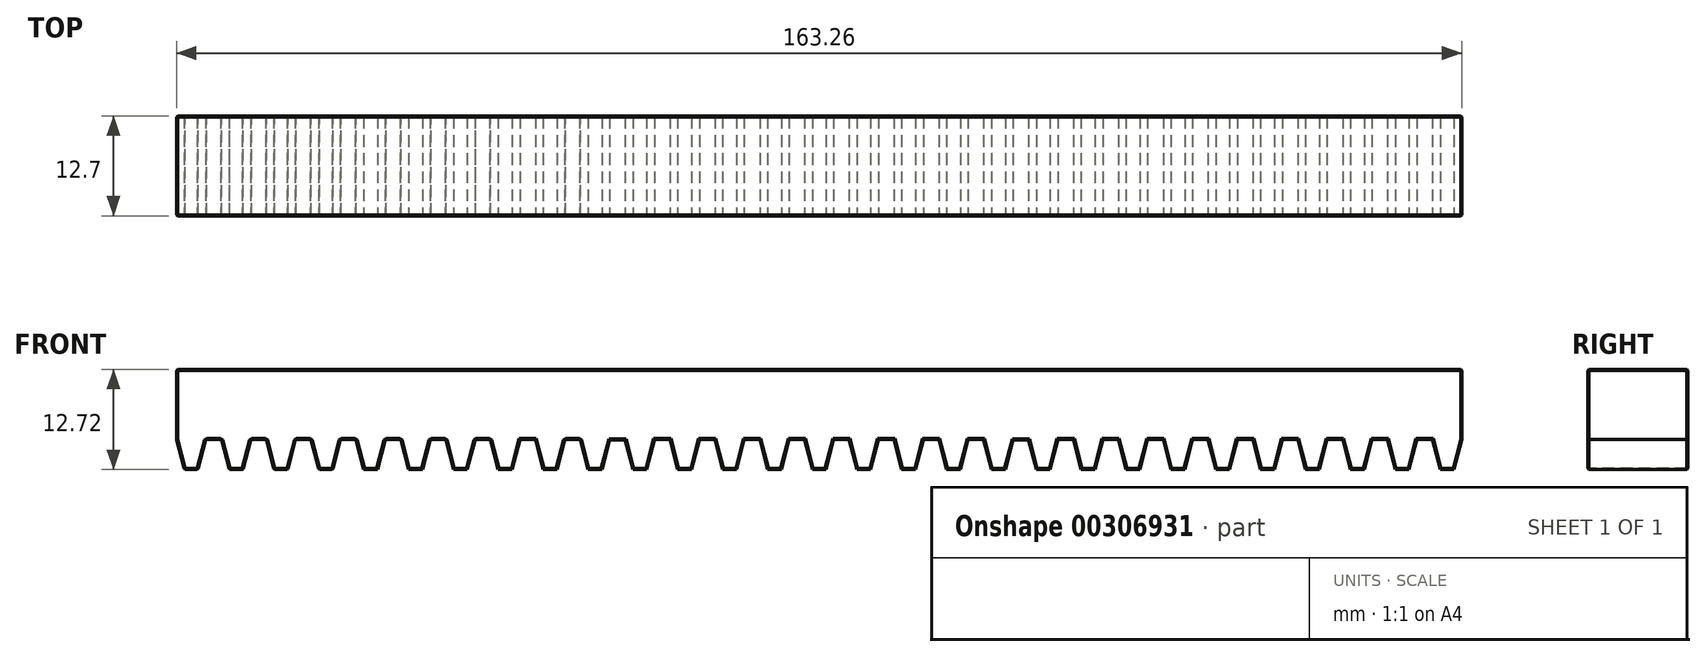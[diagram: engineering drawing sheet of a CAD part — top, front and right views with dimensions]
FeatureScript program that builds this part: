
annotation { "Feature Type Name" : "Feature", "Feature Type Description" : "" }
export const myFeature = defineFeature(function(context is Context, id is Id, definition is map)
    precondition{}
    {
        {
            var Q0;
            Q0=qCreatedBy(makeId("Front.planeOp"),FACE);
            var sketch = newSketch(context, id + "F0", { "sketchPlane" : qUnion([Q0])});
            skLineSegment(sketch, "E0.top", {"start": v(26.49, 6.35) * mm, "end": v(-136.77, 6.35) * mm});
            skLineSegment(sketch, "E0.left", {"start": v(152.4, -6.35) * mm, "end": v(152.4, 6.35) * mm});
            skPoint(sketch, "E0.middle", {"position": v(0, 0) * mm});
            skLineSegment(sketch, "E1", {"start": v(-95.96, -15.55) * mm, "end": v(-95.96, -16.34) * mm});
            skLineSegment(sketch, "E2", {"start": v(-95.96, -16.34) * mm, "end": v(-95.96, -17.1) * mm});
            skLineSegment(sketch, "E3", {"start": v(-95.96, -17.1) * mm, "end": v(-96.35, -18.17) * mm});
            skLineSegment(sketch, "E4", {"start": v(-96.35, -18.17) * mm, "end": v(-96.56, -18.75) * mm});
            skLineSegment(sketch, "E5", {"start": v(-96.56, -18.75) * mm, "end": v(-97.98, -18.75) * mm});
            skLineSegment(sketch, "E6", {"start": v(-97.98, -18.75) * mm, "end": v(-98.54, -17.62) * mm});
            skLineSegment(sketch, "E7", {"start": v(-98.54, -17.62) * mm, "end": v(-98.72, -17.01) * mm});
            skLineSegment(sketch, "E8", {"start": v(-98.72, -17.01) * mm, "end": v(-98.73, -16.25) * mm});
            skLineSegment(sketch, "E9", {"start": v(-98.73, -16.25) * mm, "end": v(-98.73, -15.44) * mm});
            skLineSegment(sketch, "E10", {"start": v(-134.03, -6.35) * mm, "end": v(-133.05, -2.54) * mm});
            skLineSegment(sketch, "E11", {"start": v(-133.05, -2.54) * mm, "end": v(-131.07, -2.54) * mm});
            skLineSegment(sketch, "E12", {"start": v(-131.07, -2.54) * mm, "end": v(-130.09, -6.35) * mm});
            skLineSegment(sketch, "E13", {"start": v(-127.35, -2.54) * mm, "end": v(-126.2, -2.54) * mm});
            skLineSegment(sketch, "E14", {"start": v(-127.35, -2.54) * mm, "end": v(-125.37, -2.54) * mm});
            skLineSegment(sketch, "E15.1.0.0", {"start": v(-124.39, -6.37) * mm, "end": v(-123.54, -6.37) * mm});
            skLineSegment(sketch, "E16", {"start": v(-128.33, -6.37) * mm, "end": v(-127.35, -2.56) * mm});
            skLineSegment(sketch, "E17", {"start": v(-127.35, -2.56) * mm, "end": v(-125.37, -2.56) * mm});
            skLineSegment(sketch, "E18", {"start": v(-125.37, -2.56) * mm, "end": v(-124.39, -6.37) * mm});
            skLineSegment(sketch, "E19", {"start": v(-123.54, -6.37) * mm, "end": v(-122.63, -6.37) * mm});
            skLineSegment(sketch, "E20.1.0.0", {"start": v(-118.69, -6.37) * mm, "end": v(-117.84, -6.37) * mm});
            skLineSegment(sketch, "E21", {"start": v(-122.63, -6.37) * mm, "end": v(-121.65, -2.56) * mm});
            skLineSegment(sketch, "E22", {"start": v(-121.65, -2.56) * mm, "end": v(-119.67, -2.56) * mm});
            skLineSegment(sketch, "E23", {"start": v(-119.67, -2.56) * mm, "end": v(-118.69, -6.37) * mm});
            skLineSegment(sketch, "E24", {"start": v(-117.84, -6.35) * mm, "end": v(-116.93, -6.37) * mm});
            skLineSegment(sketch, "E25.1.0.0", {"start": v(-112.99, -6.37) * mm, "end": v(-112.14, -6.37) * mm});
            skLineSegment(sketch, "E26", {"start": v(-116.93, -6.37) * mm, "end": v(-115.95, -2.56) * mm});
            skLineSegment(sketch, "E27", {"start": v(-115.95, -2.56) * mm, "end": v(-113.97, -2.56) * mm});
            skLineSegment(sketch, "E28", {"start": v(-113.97, -2.56) * mm, "end": v(-112.99, -6.37) * mm});
            skLineSegment(sketch, "E29", {"start": v(-136.77, -2.56) * mm, "end": v(-135.8, -6.33) * mm});
            skLineSegment(sketch, "E30", {"start": v(-112.14, -6.35) * mm, "end": v(-111.23, -6.37) * mm});
            skLineSegment(sketch, "E31.1.0.0", {"start": v(-107.3, -6.37) * mm, "end": v(-106.44, -6.37) * mm});
            skLineSegment(sketch, "E32", {"start": v(-111.23, -6.37) * mm, "end": v(-110.25, -2.56) * mm});
            skLineSegment(sketch, "E33", {"start": v(-110.25, -2.56) * mm, "end": v(-108.28, -2.56) * mm});
            skLineSegment(sketch, "E34", {"start": v(-108.28, -2.56) * mm, "end": v(-107.3, -6.37) * mm});
            skPoint(sketch, "E35.startSnap0", {"position": v(-109.26, -2.56) * mm});
            skLineSegment(sketch, "E36", {"start": v(-106.44, -6.35) * mm, "end": v(-105.53, -6.37) * mm});
            skLineSegment(sketch, "E37.1.0.0", {"start": v(-101.6, -6.37) * mm, "end": v(-100.74, -6.37) * mm});
            skLineSegment(sketch, "E38", {"start": v(-105.53, -6.37) * mm, "end": v(-104.55, -2.56) * mm});
            skLineSegment(sketch, "E39", {"start": v(-104.55, -2.56) * mm, "end": v(-102.58, -2.56) * mm});
            skLineSegment(sketch, "E40", {"start": v(-102.58, -2.56) * mm, "end": v(-101.6, -6.37) * mm});
            skPoint(sketch, "E41.startSnap0", {"position": v(-103.56, -2.56) * mm});
            skLineSegment(sketch, "E42", {"start": v(-100.74, -6.35) * mm, "end": v(-99.83, -6.37) * mm});
            skLineSegment(sketch, "E43.1.0.0", {"start": v(-95.9, -6.37) * mm, "end": v(-95.04, -6.37) * mm});
            skLineSegment(sketch, "E44", {"start": v(-99.83, -6.37) * mm, "end": v(-98.85, -2.56) * mm});
            skLineSegment(sketch, "E45", {"start": v(-98.85, -2.56) * mm, "end": v(-96.88, -2.56) * mm});
            skLineSegment(sketch, "E46", {"start": v(-96.88, -2.56) * mm, "end": v(-95.9, -6.37) * mm});
            skPoint(sketch, "E47.startSnap0", {"position": v(-97.86, -2.56) * mm});
            skLineSegment(sketch, "E48", {"start": v(-95.04, -6.35) * mm, "end": v(-94.13, -6.37) * mm});
            skLineSegment(sketch, "E49.1.0.0", {"start": v(-90.2, -6.37) * mm, "end": v(-89.34, -6.37) * mm});
            skLineSegment(sketch, "E50", {"start": v(-94.13, -6.37) * mm, "end": v(-93.15, -2.56) * mm});
            skLineSegment(sketch, "E51", {"start": v(-93.15, -2.56) * mm, "end": v(-91.18, -2.56) * mm});
            skLineSegment(sketch, "E52", {"start": v(-91.18, -2.56) * mm, "end": v(-90.2, -6.37) * mm});
            skPoint(sketch, "E53.startSnap0", {"position": v(-92.16, -2.56) * mm});
            skLineSegment(sketch, "E54", {"start": v(-89.34, -6.35) * mm, "end": v(-88.43, -6.37) * mm});
            skLineSegment(sketch, "E55.1.0.0", {"start": v(-84.5, -6.37) * mm, "end": v(-83.64, -6.37) * mm});
            skLineSegment(sketch, "E56", {"start": v(-88.43, -6.37) * mm, "end": v(-87.45, -2.56) * mm});
            skLineSegment(sketch, "E57", {"start": v(-87.45, -2.56) * mm, "end": v(-85.48, -2.56) * mm});
            skLineSegment(sketch, "E58", {"start": v(-85.48, -2.56) * mm, "end": v(-84.5, -6.37) * mm});
            skPoint(sketch, "E59.startSnap0", {"position": v(-86.46, -2.56) * mm});
            skLineSegment(sketch, "E60", {"start": v(-83.64, -6.37) * mm, "end": v(-82.73, -6.39) * mm});
            skLineSegment(sketch, "E61.1.0.0", {"start": v(-78.8, -6.39) * mm, "end": v(-77.94, -6.39) * mm});
            skLineSegment(sketch, "E62", {"start": v(-82.73, -6.39) * mm, "end": v(-81.75, -2.58) * mm});
            skLineSegment(sketch, "E63", {"start": v(-81.75, -2.58) * mm, "end": v(-79.78, -2.58) * mm});
            skLineSegment(sketch, "E64", {"start": v(-79.78, -2.58) * mm, "end": v(-78.8, -6.39) * mm});
            skPoint(sketch, "E65.startSnap0", {"position": v(-80.76, -2.58) * mm});
            skLineSegment(sketch, "E66", {"start": v(-77.94, -6.35) * mm, "end": v(-77.04, -6.37) * mm});
            skLineSegment(sketch, "E67.1.0.0", {"start": v(-73.1, -6.37) * mm, "end": v(-72.24, -6.37) * mm});
            skLineSegment(sketch, "E68", {"start": v(-77.04, -6.37) * mm, "end": v(-76.05, -2.56) * mm});
            skLineSegment(sketch, "E69", {"start": v(-76.05, -2.56) * mm, "end": v(-74.08, -2.56) * mm});
            skLineSegment(sketch, "E70", {"start": v(-74.08, -2.56) * mm, "end": v(-73.1, -6.37) * mm});
            skPoint(sketch, "E71.startSnap0", {"position": v(-75.06, -2.56) * mm});
            skLineSegment(sketch, "E72", {"start": v(-72.24, -6.35) * mm, "end": v(-71.34, -6.37) * mm});
            skLineSegment(sketch, "E73.1.0.0", {"start": v(-67.4, -6.37) * mm, "end": v(-66.54, -6.37) * mm});
            skLineSegment(sketch, "E74", {"start": v(-71.34, -6.37) * mm, "end": v(-70.35, -2.56) * mm});
            skLineSegment(sketch, "E75", {"start": v(-70.35, -2.56) * mm, "end": v(-68.38, -2.56) * mm});
            skLineSegment(sketch, "E76", {"start": v(-68.38, -2.56) * mm, "end": v(-67.4, -6.37) * mm});
            skPoint(sketch, "E77.startSnap0", {"position": v(-69.36, -2.56) * mm});
            skLineSegment(sketch, "E78", {"start": v(-66.54, -6.35) * mm, "end": v(-65.64, -6.37) * mm});
            skLineSegment(sketch, "E79.1.0.0", {"start": v(-61.7, -6.37) * mm, "end": v(-60.84, -6.37) * mm});
            skLineSegment(sketch, "E80", {"start": v(-65.64, -6.37) * mm, "end": v(-64.65, -2.56) * mm});
            skLineSegment(sketch, "E81", {"start": v(-64.65, -2.56) * mm, "end": v(-62.68, -2.56) * mm});
            skLineSegment(sketch, "E82", {"start": v(-62.68, -2.56) * mm, "end": v(-61.7, -6.37) * mm});
            skPoint(sketch, "E83.startSnap0", {"position": v(-63.66, -2.56) * mm});
            skLineSegment(sketch, "E84", {"start": v(-60.84, -6.35) * mm, "end": v(-59.94, -6.37) * mm});
            skLineSegment(sketch, "E85.1.0.0", {"start": v(-56, -6.37) * mm, "end": v(-55.14, -6.37) * mm});
            skLineSegment(sketch, "E86", {"start": v(-59.94, -6.37) * mm, "end": v(-58.95, -2.56) * mm});
            skLineSegment(sketch, "E87", {"start": v(-58.95, -2.56) * mm, "end": v(-56.98, -2.56) * mm});
            skLineSegment(sketch, "E88", {"start": v(-56.98, -2.56) * mm, "end": v(-56, -6.37) * mm});
            skPoint(sketch, "E89.startSnap0", {"position": v(-57.96, -2.56) * mm});
            skLineSegment(sketch, "E90", {"start": v(-55.14, -6.37) * mm, "end": v(-54.24, -6.39) * mm});
            skLineSegment(sketch, "E91", {"start": v(-54.24, -6.39) * mm, "end": v(-53.25, -2.58) * mm});
            skLineSegment(sketch, "E92.trimOffspring", {"start": v(-116.93, -6.35) * mm, "end": v(-117.84, -6.35) * mm});
            skLineSegment(sketch, "E93.trimOffspring", {"start": v(-111.23, -6.35) * mm, "end": v(-113, -6.35) * mm});
            skLineSegment(sketch, "E94.trimOffspring", {"start": v(-105.53, -6.35) * mm, "end": v(-107.3, -6.35) * mm});
            skLineSegment(sketch, "E95.trimOffspring", {"start": v(-99.83, -6.35) * mm, "end": v(-101.6, -6.35) * mm});
            skLineSegment(sketch, "E96.trimOffspring", {"start": v(-94.13, -6.35) * mm, "end": v(-95.9, -6.35) * mm});
            skLineSegment(sketch, "E97.trimOffspring", {"start": v(-88.43, -6.35) * mm, "end": v(-90.2, -6.35) * mm});
            skLineSegment(sketch, "E98.trimOffspring", {"start": v(-82.73, -6.35) * mm, "end": v(-84.5, -6.35) * mm});
            skLineSegment(sketch, "E99.trimOffspring", {"start": v(-77.03, -6.35) * mm, "end": v(-78.8, -6.35) * mm});
            skLineSegment(sketch, "E100.trimOffspring", {"start": v(-71.33, -6.35) * mm, "end": v(-73.1, -6.35) * mm});
            skLineSegment(sketch, "E101.trimOffspring", {"start": v(-65.63, -6.35) * mm, "end": v(-67.4, -6.35) * mm});
            skLineSegment(sketch, "E102.trimOffspring", {"start": v(-59.93, -6.35) * mm, "end": v(-61.7, -6.35) * mm});
            skLineSegment(sketch, "E103.trimOffspring", {"start": v(-54.23, -6.35) * mm, "end": v(-56, -6.35) * mm});
            skLineSegment(sketch, "E104.trimOffspring", {"start": v(-124.4, -6.35) * mm, "end": v(-122.63, -6.35) * mm});
            skLineSegment(sketch, "E105.trimOffspring", {"start": v(-118.7, -6.35) * mm, "end": v(-116.93, -6.35) * mm});
            skLineSegment(sketch, "E106.trimOffspring", {"start": v(-113, -6.35) * mm, "end": v(-111.23, -6.35) * mm});
            skLineSegment(sketch, "E107.trimOffspring", {"start": v(-107.3, -6.35) * mm, "end": v(-105.53, -6.35) * mm});
            skLineSegment(sketch, "E108.trimOffspring", {"start": v(-101.6, -6.35) * mm, "end": v(-99.83, -6.35) * mm});
            skLineSegment(sketch, "E109.trimOffspring", {"start": v(-95.9, -6.35) * mm, "end": v(-94.13, -6.35) * mm});
            skLineSegment(sketch, "E110.trimOffspring", {"start": v(-90.2, -6.35) * mm, "end": v(-88.43, -6.35) * mm});
            skLineSegment(sketch, "E111.trimOffspring", {"start": v(-84.5, -6.35) * mm, "end": v(-82.73, -6.35) * mm});
            skLineSegment(sketch, "E112.trimOffspring", {"start": v(-78.8, -6.35) * mm, "end": v(-77.03, -6.35) * mm});
            skLineSegment(sketch, "E113.trimOffspring", {"start": v(-73.1, -6.35) * mm, "end": v(-71.33, -6.35) * mm});
            skLineSegment(sketch, "E114.trimOffspring", {"start": v(-67.4, -6.35) * mm, "end": v(-65.63, -6.35) * mm});
            skLineSegment(sketch, "E115.trimOffspring", {"start": v(-61.7, -6.35) * mm, "end": v(-59.93, -6.35) * mm});
            skLineSegment(sketch, "E116.trimOffspring", {"start": v(-56, -6.35) * mm, "end": v(-54.23, -6.35) * mm});
            skLineSegment(sketch, "E117", {"start": v(-136.77, -2.56) * mm, "end": v(-136.77, 6.35) * mm});
            skLineSegment(sketch, "E118", {"start": v(-53.25, -2.58) * mm, "end": v(-53.25, -2.56) * mm});
            skLineSegment(sketch, "E119", {"start": v(-135.8, -6.33) * mm, "end": v(-134.03, -6.35) * mm});
            skLineSegment(sketch, "E120", {"start": v(-130.09, -6.35) * mm, "end": v(-128.33, -6.37) * mm});
            skLineSegment(sketch, "E121", {"start": v(-133.78, -3.12) * mm, "end": v(-133.78, -3.91) * mm});
            skLineSegment(sketch, "E122", {"start": v(-133.78, -3.91) * mm, "end": v(-133.78, -4.68) * mm});
            skLineSegment(sketch, "E123", {"start": v(-133.78, -4.68) * mm, "end": v(-134.17, -5.75) * mm});
            skLineSegment(sketch, "E124", {"start": v(-134.17, -5.75) * mm, "end": v(-134.38, -6.33) * mm});
            skLineSegment(sketch, "E125", {"start": v(-134.38, -6.33) * mm, "end": v(-135.8, -6.33) * mm});
            skLineSegment(sketch, "E126", {"start": v(-135.8, -6.33) * mm, "end": v(-136.36, -5.2) * mm});
            skLineSegment(sketch, "E127", {"start": v(-136.36, -5.2) * mm, "end": v(-136.54, -4.6) * mm});
            skLineSegment(sketch, "E128", {"start": v(-136.54, -4.6) * mm, "end": v(-136.55, -3.83) * mm});
            skLineSegment(sketch, "E129", {"start": v(-136.55, -3.83) * mm, "end": v(-136.55, -3.01) * mm});
            skLineSegment(sketch, "E130", {"start": v(-128.08, -3.14) * mm, "end": v(-128.07, -3.93) * mm});
            skLineSegment(sketch, "E131", {"start": v(-128.07, -3.93) * mm, "end": v(-128.07, -4.7) * mm});
            skLineSegment(sketch, "E132", {"start": v(-128.07, -4.7) * mm, "end": v(-128.47, -5.76) * mm});
            skLineSegment(sketch, "E133", {"start": v(-128.47, -5.76) * mm, "end": v(-128.67, -6.35) * mm});
            skLineSegment(sketch, "E134", {"start": v(-128.67, -6.35) * mm, "end": v(-130.09, -6.35) * mm});
            skLineSegment(sketch, "E135", {"start": v(-130.09, -6.35) * mm, "end": v(-130.65, -5.21) * mm});
            skLineSegment(sketch, "E136", {"start": v(-130.65, -5.21) * mm, "end": v(-130.84, -4.6) * mm});
            skLineSegment(sketch, "E137", {"start": v(-130.84, -4.6) * mm, "end": v(-130.84, -3.84) * mm});
            skLineSegment(sketch, "E138", {"start": v(-130.84, -3.84) * mm, "end": v(-130.84, -3.03) * mm});
            skLineSegment(sketch, "E139", {"start": v(-122.38, -3.16) * mm, "end": v(-122.37, -3.95) * mm});
            skLineSegment(sketch, "E140", {"start": v(-122.37, -3.95) * mm, "end": v(-122.37, -4.71) * mm});
            skLineSegment(sketch, "E141", {"start": v(-122.37, -4.71) * mm, "end": v(-122.77, -5.78) * mm});
            skLineSegment(sketch, "E142", {"start": v(-122.77, -5.78) * mm, "end": v(-122.97, -6.36) * mm});
            skLineSegment(sketch, "E143", {"start": v(-122.97, -6.36) * mm, "end": v(-124.39, -6.37) * mm});
            skLineSegment(sketch, "E144", {"start": v(-124.39, -6.37) * mm, "end": v(-124.95, -5.23) * mm});
            skLineSegment(sketch, "E145", {"start": v(-124.95, -5.23) * mm, "end": v(-125.14, -4.63) * mm});
            skLineSegment(sketch, "E146", {"start": v(-125.14, -4.63) * mm, "end": v(-125.14, -3.86) * mm});
            skLineSegment(sketch, "E147", {"start": v(-125.14, -3.86) * mm, "end": v(-125.14, -3.05) * mm});
            skLineSegment(sketch, "E148", {"start": v(-116.68, -3.16) * mm, "end": v(-116.67, -3.95) * mm});
            skLineSegment(sketch, "E149", {"start": v(-116.67, -3.95) * mm, "end": v(-116.67, -4.72) * mm});
            skLineSegment(sketch, "E150", {"start": v(-116.67, -4.72) * mm, "end": v(-117.07, -5.79) * mm});
            skLineSegment(sketch, "E151", {"start": v(-117.07, -5.79) * mm, "end": v(-117.27, -6.37) * mm});
            skLineSegment(sketch, "E152", {"start": v(-117.27, -6.37) * mm, "end": v(-118.69, -6.37) * mm});
            skLineSegment(sketch, "E153", {"start": v(-118.69, -6.37) * mm, "end": v(-119.25, -5.23) * mm});
            skLineSegment(sketch, "E154", {"start": v(-119.25, -5.23) * mm, "end": v(-119.44, -4.63) * mm});
            skLineSegment(sketch, "E155", {"start": v(-119.44, -4.63) * mm, "end": v(-119.44, -3.86) * mm});
            skLineSegment(sketch, "E156", {"start": v(-119.44, -3.86) * mm, "end": v(-119.44, -3.05) * mm});
            skLineSegment(sketch, "E157.MirrorCS", {"start": v(-31.48, -6.35) * mm, "end": v(-33.26, -6.35) * mm});
            skLineSegment(sketch, "E158.MirrorCS", {"start": v(-31.5, -6.39) * mm, "end": v(-32.34, -6.39) * mm});
            skLineSegment(sketch, "E159.MirrorCS", {"start": v(-14.4, -6.35) * mm, "end": v(-16.16, -6.35) * mm});
            skLineSegment(sketch, "E160.MirrorCS", {"start": v(-37.19, -6.35) * mm, "end": v(-38.96, -6.35) * mm});
            skLineSegment(sketch, "E161.MirrorCS", {"start": v(-4.76, -6.35) * mm, "end": v(-3, -6.35) * mm});
            skLineSegment(sketch, "E162.MirrorCS", {"start": v(-8.7, -6.37) * mm, "end": v(-9.54, -6.37) * mm});
            skLineSegment(sketch, "E163.MirrorCS", {"start": v(-20.09, -6.35) * mm, "end": v(-21.86, -6.35) * mm});
            skLineSegment(sketch, "E164.MirrorCS", {"start": v(-16.16, -6.35) * mm, "end": v(-14.4, -6.35) * mm});
            skLineSegment(sketch, "E165.MirrorCS", {"start": v(-42.89, -6.35) * mm, "end": v(-44.65, -6.35) * mm});
            skLineSegment(sketch, "E166.MirrorCS", {"start": v(-38.96, -6.35) * mm, "end": v(-37.19, -6.35) * mm});
            skLineSegment(sketch, "E167.MirrorCS", {"start": v(8.4, -6.35) * mm, "end": v(6.64, -6.35) * mm});
            skLineSegment(sketch, "E168.MirrorCS", {"start": v(-42.9, -6.37) * mm, "end": v(-43.74, -6.37) * mm});
            skLineSegment(sketch, "E169.MirrorCS", {"start": v(-20.94, -6.35) * mm, "end": v(-21.85, -6.37) * mm});
            skLineSegment(sketch, "E170.MirrorCS", {"start": v(-8.7, -6.35) * mm, "end": v(-10.46, -6.35) * mm});
            skLineSegment(sketch, "E171.MirrorCS", {"start": v(0.94, -6.35) * mm, "end": v(2.7, -6.35) * mm});
            skLineSegment(sketch, "E172.MirrorCS", {"start": v(-25.8, -6.37) * mm, "end": v(-26.64, -6.37) * mm});
            skLineSegment(sketch, "E173.MirrorCS", {"start": v(-3.85, -6.35) * mm, "end": v(-4.75, -6.37) * mm});
            skLineSegment(sketch, "E174.MirrorCS", {"start": v(-25.79, -6.35) * mm, "end": v(-27.56, -6.35) * mm});
            skLineSegment(sketch, "E175.MirrorCS", {"start": v(-48.6, -6.37) * mm, "end": v(-49.44, -6.37) * mm});
            skLineSegment(sketch, "E176.MirrorCS", {"start": v(2.7, -6.37) * mm, "end": v(1.85, -6.37) * mm});
            skLineSegment(sketch, "E177.MirrorCS", {"start": v(-48.59, -6.35) * mm, "end": v(-50.35, -6.35) * mm});
            skLineSegment(sketch, "E178.MirrorCS", {"start": v(-33.26, -6.35) * mm, "end": v(-31.48, -6.35) * mm});
            skLineSegment(sketch, "E179.MirrorCS", {"start": v(-32.34, -6.35) * mm, "end": v(-33.25, -6.37) * mm});
            skLineSegment(sketch, "E180.MirrorCS", {"start": v(-10.46, -6.35) * mm, "end": v(-8.7, -6.35) * mm});
            skLineSegment(sketch, "E181.MirrorCS", {"start": v(-43.74, -6.35) * mm, "end": v(-44.65, -6.37) * mm});
            skLineSegment(sketch, "E182.MirrorCS", {"start": v(-27.56, -6.35) * mm, "end": v(-25.79, -6.35) * mm});
            skLineSegment(sketch, "E183.MirrorCS", {"start": v(-50.35, -6.35) * mm, "end": v(-48.59, -6.35) * mm});
            skLineSegment(sketch, "E184.MirrorCS", {"start": v(-44.65, -6.35) * mm, "end": v(-42.89, -6.35) * mm});
            skLineSegment(sketch, "E185.MirrorCS", {"start": v(-49.44, -6.35) * mm, "end": v(-50.35, -6.37) * mm});
            skLineSegment(sketch, "E186.MirrorCS", {"start": v(-37.2, -6.37) * mm, "end": v(-38.04, -6.37) * mm});
            skLineSegment(sketch, "E187.MirrorCS", {"start": v(-15.24, -6.35) * mm, "end": v(-16.15, -6.37) * mm});
            skLineSegment(sketch, "E188.MirrorCS", {"start": v(25.51, -6.33) * mm, "end": v(23.75, -6.35) * mm});
            skLineSegment(sketch, "E189.MirrorCS", {"start": v(-20.1, -6.37) * mm, "end": v(-20.94, -6.37) * mm});
            skLineSegment(sketch, "E190.MirrorCS", {"start": v(1.85, -6.35) * mm, "end": v(0.95, -6.37) * mm});
            skLineSegment(sketch, "E191.MirrorCS", {"start": v(19.8, -6.35) * mm, "end": v(18.05, -6.37) * mm});
            skLineSegment(sketch, "E192.MirrorCS", {"start": v(14.1, -6.35) * mm, "end": v(12.34, -6.35) * mm});
            skLineSegment(sketch, "E193.MirrorCS", {"start": v(-3, -6.37) * mm, "end": v(-3.85, -6.37) * mm});
            skLineSegment(sketch, "E194.MirrorCS", {"start": v(2.7, -6.35) * mm, "end": v(0.94, -6.35) * mm});
            skLineSegment(sketch, "E195.MirrorCS", {"start": v(-38.04, -6.35) * mm, "end": v(-38.95, -6.37) * mm});
            skLineSegment(sketch, "E196.MirrorCS", {"start": v(-26.64, -6.37) * mm, "end": v(-27.55, -6.39) * mm});
            skLineSegment(sketch, "E197.MirrorCS", {"start": v(-21.86, -6.35) * mm, "end": v(-20.09, -6.35) * mm});
            skLineSegment(sketch, "E198.MirrorCS", {"start": v(-9.54, -6.35) * mm, "end": v(-10.45, -6.37) * mm});
            skLineSegment(sketch, "E199.MirrorCS", {"start": v(-14.4, -6.37) * mm, "end": v(-15.24, -6.37) * mm});
            skLineSegment(sketch, "E200.MirrorCS", {"start": v(-54.3, -6.37) * mm, "end": v(-55.14, -6.37) * mm});
            skLineSegment(sketch, "E201.MirrorCS", {"start": v(-3, -6.35) * mm, "end": v(-4.76, -6.35) * mm});
            skLineSegment(sketch, "E202.MirrorCS", {"start": v(17.06, -2.54) * mm, "end": v(15.9, -2.54) * mm});
            skLineSegment(sketch, "E203.MirrorCS", {"start": v(15.09, -2.56) * mm, "end": v(14.1, -6.37) * mm});
            skLineSegment(sketch, "E204.MirrorCS", {"start": v(-39.93, -2.56) * mm, "end": v(-41.9, -2.56) * mm});
            skLineSegment(sketch, "E205.MirrorCS", {"start": v(12.35, -6.37) * mm, "end": v(11.36, -2.56) * mm});
            skLineSegment(sketch, "E206.MirrorCS", {"start": v(-22.84, -2.56) * mm, "end": v(-24.8, -2.56) * mm});
            skLineSegment(sketch, "E207.MirrorCS", {"start": v(-5.74, -2.56) * mm, "end": v(-7.71, -2.56) * mm});
            skLineSegment(sketch, "E208.MirrorCS", {"start": v(11.36, -2.56) * mm, "end": v(9.39, -2.56) * mm});
            skLineSegment(sketch, "E209.MirrorCS", {"start": v(-28.54, -2.58) * mm, "end": v(-30.5, -2.58) * mm});
            skLineSegment(sketch, "E210.MirrorCS", {"start": v(6.65, -6.37) * mm, "end": v(5.66, -2.56) * mm});
            skLineSegment(sketch, "E211.MirrorCS", {"start": v(-11.44, -2.56) * mm, "end": v(-13.41, -2.56) * mm});
            skLineSegment(sketch, "E212.MirrorCS", {"start": v(5.66, -2.56) * mm, "end": v(3.69, -2.56) * mm});
            skLineSegment(sketch, "E213.MirrorCS", {"start": v(26.49, -2.56) * mm, "end": v(25.51, -6.33) * mm});
            skLineSegment(sketch, "E214.MirrorCS", {"start": v(-51.33, -2.56) * mm, "end": v(-53.3, -2.56) * mm});
            skLineSegment(sketch, "E215.MirrorCS", {"start": v(20.79, -2.54) * mm, "end": v(19.8, -6.35) * mm});
            skLineSegment(sketch, "E216.MirrorCS", {"start": v(17.06, -2.54) * mm, "end": v(15.09, -2.54) * mm});
            skLineSegment(sketch, "E217.MirrorCS", {"start": v(23.75, -6.35) * mm, "end": v(22.76, -2.54) * mm});
            skLineSegment(sketch, "E218.MirrorCS", {"start": v(22.76, -2.54) * mm, "end": v(20.79, -2.54) * mm});
            skLineSegment(sketch, "E219.MirrorCS", {"start": v(-34.24, -2.56) * mm, "end": v(-36.2, -2.56) * mm});
            skLineSegment(sketch, "E220.MirrorCS", {"start": v(18.05, -6.37) * mm, "end": v(17.06, -2.56) * mm});
            skLineSegment(sketch, "E221.MirrorCS", {"start": v(-17.14, -2.56) * mm, "end": v(-19.11, -2.56) * mm});
            skLineSegment(sketch, "E222.MirrorCS", {"start": v(17.06, -2.56) * mm, "end": v(15.09, -2.56) * mm});
            skLineSegment(sketch, "E223.MirrorCS", {"start": v(-0.04, -2.56) * mm, "end": v(-2.01, -2.56) * mm});
            skLineSegment(sketch, "E224.MirrorCS", {"start": v(9.39, -2.56) * mm, "end": v(8.4, -6.37) * mm});
            skLineSegment(sketch, "E225.MirrorCS", {"start": v(-45.63, -2.56) * mm, "end": v(-47.6, -2.56) * mm});
            skLineSegment(sketch, "E226.MirrorCS", {"start": v(-21.85, -6.37) * mm, "end": v(-22.84, -2.56) * mm});
            skLineSegment(sketch, "E227.MirrorCS", {"start": v(-41.9, -2.56) * mm, "end": v(-42.9, -6.37) * mm});
            skLineSegment(sketch, "E228.MirrorCS", {"start": v(-4.75, -6.37) * mm, "end": v(-5.74, -2.56) * mm});
            skLineSegment(sketch, "E229.MirrorCS", {"start": v(-24.8, -2.56) * mm, "end": v(-25.8, -6.37) * mm});
            skPoint(sketch, "E230.MirrorP", {"position": v(-12.42, -2.56) * mm});
            skLineSegment(sketch, "E231.MirrorCS", {"start": v(-10.45, -6.37) * mm, "end": v(-11.44, -2.56) * mm});
            skLineSegment(sketch, "E232.MirrorCS", {"start": v(-47.6, -2.56) * mm, "end": v(-48.6, -6.37) * mm});
            skPoint(sketch, "E233.MirrorP", {"position": v(-1.02, -2.56) * mm});
            skPoint(sketch, "E234.MirrorP", {"position": v(-18.12, -2.56) * mm});
            skLineSegment(sketch, "E235.MirrorCS", {"start": v(-30.5, -2.58) * mm, "end": v(-31.5, -6.39) * mm});
            skLineSegment(sketch, "E236.MirrorCS", {"start": v(26.49, -2.56) * mm, "end": v(26.49, 6.35) * mm});
            skLineSegment(sketch, "E237.MirrorCS", {"start": v(-50.35, -6.37) * mm, "end": v(-51.33, -2.56) * mm});
            skPoint(sketch, "E238.MirrorP", {"position": v(-6.72, -2.56) * mm});
            skPoint(sketch, "E239.MirrorP", {"position": v(-23.82, -2.56) * mm});
            skLineSegment(sketch, "E240.MirrorCS", {"start": v(-33.25, -6.37) * mm, "end": v(-34.24, -2.56) * mm});
            skPoint(sketch, "E241.MirrorP", {"position": v(-29.52, -2.58) * mm});
            skLineSegment(sketch, "E242.MirrorCS", {"start": v(-53.3, -2.56) * mm, "end": v(-54.3, -6.37) * mm});
            skLineSegment(sketch, "E243.MirrorCS", {"start": v(-16.15, -6.37) * mm, "end": v(-17.14, -2.56) * mm});
            skPoint(sketch, "E244.MirrorP", {"position": v(-35.22, -2.56) * mm});
            skLineSegment(sketch, "E245.MirrorCS", {"start": v(-36.2, -2.56) * mm, "end": v(-37.2, -6.37) * mm});
            skLineSegment(sketch, "E246.MirrorCS", {"start": v(0.95, -6.37) * mm, "end": v(-0.04, -2.56) * mm});
            skPoint(sketch, "E247.MirrorP", {"position": v(-40.92, -2.56) * mm});
            skLineSegment(sketch, "E248.MirrorCS", {"start": v(-19.11, -2.56) * mm, "end": v(-20.1, -6.37) * mm});
            skPoint(sketch, "E249.MirrorP", {"position": v(-46.62, -2.56) * mm});
            skLineSegment(sketch, "E250.MirrorCS", {"start": v(-2.01, -2.56) * mm, "end": v(-3, -6.37) * mm});
            skPoint(sketch, "E251.MirrorP", {"position": v(-52.32, -2.56) * mm});
            skLineSegment(sketch, "E252.MirrorCS", {"start": v(-38.95, -6.37) * mm, "end": v(-39.93, -2.56) * mm});
            skLineSegment(sketch, "E253.MirrorCS", {"start": v(-7.71, -2.56) * mm, "end": v(-8.7, -6.37) * mm});
            skLineSegment(sketch, "E254.MirrorCS", {"start": v(-44.65, -6.37) * mm, "end": v(-45.63, -2.56) * mm});
            skLineSegment(sketch, "E255.MirrorCS", {"start": v(-27.55, -6.39) * mm, "end": v(-28.54, -2.58) * mm});
            skLineSegment(sketch, "E256.MirrorCS", {"start": v(-13.41, -2.56) * mm, "end": v(-14.4, -6.37) * mm});
            skLineSegment(sketch, "E257.MirrorCS", {"start": v(3.69, -2.56) * mm, "end": v(2.7, -6.37) * mm});
            skSolve(sketch);
        }
        {
            var Q0;
            Q0=makeQuery(id+"F0.imprint","IMPRINT",FACE,{"disambiguationData":[TD([[makeQuery(id+"F0.imprint","IMPRINT",EDGE,{"derivedFrom":sQuery(id+"F0.wireOp",EDGE,"E0.top")}),1.0]])]});
            extrude(context, id + "F1", {"entities" : qUnion([Q0]), "oppositeDirection" : true, "depth" : 12.7 * mm});
        }
        {
            var Q0;
            Q0=makeQuery(id+"F1.opExtrude","CAP_FACE",FACE,{"disambiguationData":[OSD([sQuery(id+"F0.wireOp",EDGE,"E0.top"),sQuery(id+"F0.wireOp",EDGE,"E10"),sQuery(id+"F0.wireOp",EDGE,"E11"),sQuery(id+"F0.wireOp",EDGE,"E12"),sQuery(id+"F0.wireOp",EDGE,"E16"),sQuery(id+"F0.wireOp",EDGE,"E17"),sQuery(id+"F0.wireOp",EDGE,"E18"),sQuery(id+"F0.wireOp",EDGE,"E21"),sQuery(id+"F0.wireOp",EDGE,"E22"),sQuery(id+"F0.wireOp",EDGE,"E23"),sQuery(id+"F0.wireOp",EDGE,"E26"),sQuery(id+"F0.wireOp",EDGE,"E27"),sQuery(id+"F0.wireOp",EDGE,"E28"),sQuery(id+"F0.wireOp",EDGE,"E29"),sQuery(id+"F0.wireOp",EDGE,"E32"),sQuery(id+"F0.wireOp",EDGE,"E33"),sQuery(id+"F0.wireOp",EDGE,"E34"),sQuery(id+"F0.wireOp",EDGE,"E38"),sQuery(id+"F0.wireOp",EDGE,"E39"),sQuery(id+"F0.wireOp",EDGE,"E40"),sQuery(id+"F0.wireOp",EDGE,"E44"),sQuery(id+"F0.wireOp",EDGE,"E45"),sQuery(id+"F0.wireOp",EDGE,"E46"),sQuery(id+"F0.wireOp",EDGE,"E50"),sQuery(id+"F0.wireOp",EDGE,"E51"),sQuery(id+"F0.wireOp",EDGE,"E52"),sQuery(id+"F0.wireOp",EDGE,"E56"),sQuery(id+"F0.wireOp",EDGE,"E57"),sQuery(id+"F0.wireOp",EDGE,"E58"),sQuery(id+"F0.wireOp",EDGE,"E62"),sQuery(id+"F0.wireOp",EDGE,"E63"),sQuery(id+"F0.wireOp",EDGE,"E64"),sQuery(id+"F0.wireOp",EDGE,"E68"),sQuery(id+"F0.wireOp",EDGE,"E69"),sQuery(id+"F0.wireOp",EDGE,"E70"),sQuery(id+"F0.wireOp",EDGE,"E74"),sQuery(id+"F0.wireOp",EDGE,"E75"),sQuery(id+"F0.wireOp",EDGE,"E76"),sQuery(id+"F0.wireOp",EDGE,"E80"),sQuery(id+"F0.wireOp",EDGE,"E81"),sQuery(id+"F0.wireOp",EDGE,"E82"),sQuery(id+"F0.wireOp",EDGE,"E86"),sQuery(id+"F0.wireOp",EDGE,"E87"),sQuery(id+"F0.wireOp",EDGE,"E88"),sQuery(id+"F0.wireOp",EDGE,"E91"),sQuery(id+"F0.wireOp",EDGE,"E104.trimOffspring"),sQuery(id+"F0.wireOp",EDGE,"E105.trimOffspring"),sQuery(id+"F0.wireOp",EDGE,"E106.trimOffspring"),sQuery(id+"F0.wireOp",EDGE,"E107.trimOffspring"),sQuery(id+"F0.wireOp",EDGE,"E108.trimOffspring"),sQuery(id+"F0.wireOp",EDGE,"E109.trimOffspring"),sQuery(id+"F0.wireOp",EDGE,"E110.trimOffspring"),sQuery(id+"F0.wireOp",EDGE,"E111.trimOffspring"),sQuery(id+"F0.wireOp",EDGE,"E112.trimOffspring"),sQuery(id+"F0.wireOp",EDGE,"E113.trimOffspring"),sQuery(id+"F0.wireOp",EDGE,"E114.trimOffspring"),sQuery(id+"F0.wireOp",EDGE,"E115.trimOffspring"),sQuery(id+"F0.wireOp",EDGE,"E116.trimOffspring"),sQuery(id+"F0.wireOp",EDGE,"E117"),sQuery(id+"F0.wireOp",EDGE,"E118"),sQuery(id+"F0.wireOp",EDGE,"E119"),sQuery(id+"F0.wireOp",EDGE,"E120")])],"isStart":true});
            var Q1;
            Q1=makeQuery(id+"F1.opExtrude","CAP_FACE",FACE,{"disambiguationData":[OSD([sQuery(id+"F0.wireOp",EDGE,"E0.top"),sQuery(id+"F0.wireOp",EDGE,"E10"),sQuery(id+"F0.wireOp",EDGE,"E11"),sQuery(id+"F0.wireOp",EDGE,"E12"),sQuery(id+"F0.wireOp",EDGE,"E16"),sQuery(id+"F0.wireOp",EDGE,"E17"),sQuery(id+"F0.wireOp",EDGE,"E18"),sQuery(id+"F0.wireOp",EDGE,"E21"),sQuery(id+"F0.wireOp",EDGE,"E22"),sQuery(id+"F0.wireOp",EDGE,"E23"),sQuery(id+"F0.wireOp",EDGE,"E26"),sQuery(id+"F0.wireOp",EDGE,"E27"),sQuery(id+"F0.wireOp",EDGE,"E28"),sQuery(id+"F0.wireOp",EDGE,"E29"),sQuery(id+"F0.wireOp",EDGE,"E32"),sQuery(id+"F0.wireOp",EDGE,"E33"),sQuery(id+"F0.wireOp",EDGE,"E34"),sQuery(id+"F0.wireOp",EDGE,"E38"),sQuery(id+"F0.wireOp",EDGE,"E39"),sQuery(id+"F0.wireOp",EDGE,"E40"),sQuery(id+"F0.wireOp",EDGE,"E44"),sQuery(id+"F0.wireOp",EDGE,"E45"),sQuery(id+"F0.wireOp",EDGE,"E46"),sQuery(id+"F0.wireOp",EDGE,"E50"),sQuery(id+"F0.wireOp",EDGE,"E51"),sQuery(id+"F0.wireOp",EDGE,"E52"),sQuery(id+"F0.wireOp",EDGE,"E56"),sQuery(id+"F0.wireOp",EDGE,"E57"),sQuery(id+"F0.wireOp",EDGE,"E58"),sQuery(id+"F0.wireOp",EDGE,"E62"),sQuery(id+"F0.wireOp",EDGE,"E63"),sQuery(id+"F0.wireOp",EDGE,"E64"),sQuery(id+"F0.wireOp",EDGE,"E68"),sQuery(id+"F0.wireOp",EDGE,"E69"),sQuery(id+"F0.wireOp",EDGE,"E70"),sQuery(id+"F0.wireOp",EDGE,"E74"),sQuery(id+"F0.wireOp",EDGE,"E75"),sQuery(id+"F0.wireOp",EDGE,"E76"),sQuery(id+"F0.wireOp",EDGE,"E80"),sQuery(id+"F0.wireOp",EDGE,"E81"),sQuery(id+"F0.wireOp",EDGE,"E82"),sQuery(id+"F0.wireOp",EDGE,"E86"),sQuery(id+"F0.wireOp",EDGE,"E87"),sQuery(id+"F0.wireOp",EDGE,"E88"),sQuery(id+"F0.wireOp",EDGE,"E91"),sQuery(id+"F0.wireOp",EDGE,"E104.trimOffspring"),sQuery(id+"F0.wireOp",EDGE,"E105.trimOffspring"),sQuery(id+"F0.wireOp",EDGE,"E106.trimOffspring"),sQuery(id+"F0.wireOp",EDGE,"E107.trimOffspring"),sQuery(id+"F0.wireOp",EDGE,"E108.trimOffspring"),sQuery(id+"F0.wireOp",EDGE,"E109.trimOffspring"),sQuery(id+"F0.wireOp",EDGE,"E110.trimOffspring"),sQuery(id+"F0.wireOp",EDGE,"E111.trimOffspring"),sQuery(id+"F0.wireOp",EDGE,"E112.trimOffspring"),sQuery(id+"F0.wireOp",EDGE,"E113.trimOffspring"),sQuery(id+"F0.wireOp",EDGE,"E114.trimOffspring"),sQuery(id+"F0.wireOp",EDGE,"E115.trimOffspring"),sQuery(id+"F0.wireOp",EDGE,"E116.trimOffspring"),sQuery(id+"F0.wireOp",EDGE,"E117"),sQuery(id+"F0.wireOp",EDGE,"E118"),sQuery(id+"F0.wireOp",EDGE,"E119"),sQuery(id+"F0.wireOp",EDGE,"E120")])],"isStart":false});
            var Q2;
            Q2=makeQuery(id+"F1.opExtrude","SWEPT_FACE",FACE,{"disambiguationData":[OSD([sQuery(id+"F0.wireOp",EDGE,"E118")])]});
            var Q3;
            Q3=makeQuery(id+"F1.opExtrude","SWEPT_FACE",FACE,{"disambiguationData":[OSD([sQuery(id+"F0.wireOp",EDGE,"E0.top")])]});
            var Q4;
            Q4=makeQuery(id+"F1.opExtrude","SWEPT_FACE",FACE,{"disambiguationData":[OSD([sQuery(id+"F0.wireOp",EDGE,"E117")])]});
            var Q5;
            Q5=makeQuery(id+"F1.opExtrude","SWEPT_FACE",FACE,{"disambiguationData":[OSD([sQuery(id+"F0.wireOp",EDGE,"E119")])]});
            var Q6;
            Q6=makeQuery(id+"F1.opExtrude","SWEPT_FACE",FACE,{"disambiguationData":[OSD([sQuery(id+"F0.wireOp",EDGE,"E11")])]});
            var Q7;
            Q7=makeQuery(id+"F1.opExtrude","SWEPT_FACE",FACE,{"disambiguationData":[OSD([sQuery(id+"F0.wireOp",EDGE,"E120")])]});
            var Q8;
            Q8=makeQuery(id+"F1.opExtrude","SWEPT_FACE",FACE,{"disambiguationData":[OSD([sQuery(id+"F0.wireOp",EDGE,"E17")])]});
            var Q9;
            Q9=makeQuery(id+"F1.opExtrude","SWEPT_FACE",FACE,{"disambiguationData":[OSD([sQuery(id+"F0.wireOp",EDGE,"E104.trimOffspring")])]});
            var Q10;
            Q10=makeQuery(id+"F1.opExtrude","SWEPT_FACE",FACE,{"disambiguationData":[OSD([sQuery(id+"F0.wireOp",EDGE,"E22")])]});
            var Q11;
            Q11=makeQuery(id+"F1.opExtrude","SWEPT_FACE",FACE,{"disambiguationData":[OSD([sQuery(id+"F0.wireOp",EDGE,"E105.trimOffspring")])]});
            var Q12;
            Q12=makeQuery(id+"F1.opExtrude","SWEPT_FACE",FACE,{"disambiguationData":[OSD([sQuery(id+"F0.wireOp",EDGE,"E27")])]});
            var Q13;
            Q13=makeQuery(id+"F1.opExtrude","SWEPT_FACE",FACE,{"disambiguationData":[OSD([sQuery(id+"F0.wireOp",EDGE,"E106.trimOffspring")])]});
            var Q14;
            Q14=makeQuery(id+"F1.opExtrude","SWEPT_EDGE",EDGE,{"disambiguationData":[OSD([sQuery(id+"F0.wireOp",EDGE,"E32"),sQuery(id+"F0.wireOp",EDGE,"E33")])]});
            var Q15;
            Q15=makeQuery(id+"F1.opExtrude","SWEPT_FACE",FACE,{"disambiguationData":[OSD([sQuery(id+"F0.wireOp",EDGE,"E33")])]});
            var Q16;
            Q16=makeQuery(id+"F1.opExtrude","SWEPT_FACE",FACE,{"disambiguationData":[OSD([sQuery(id+"F0.wireOp",EDGE,"E107.trimOffspring")])]});
            var Q17;
            Q17=makeQuery(id+"F1.opExtrude","SWEPT_FACE",FACE,{"disambiguationData":[OSD([sQuery(id+"F0.wireOp",EDGE,"E39")])]});
            var Q18;
            Q18=makeQuery(id+"F1.opExtrude","SWEPT_FACE",FACE,{"disambiguationData":[OSD([sQuery(id+"F0.wireOp",EDGE,"E108.trimOffspring")])]});
            var Q19;
            Q19=makeQuery(id+"F1.opExtrude","SWEPT_FACE",FACE,{"disambiguationData":[OSD([sQuery(id+"F0.wireOp",EDGE,"E45")])]});
            var Q20;
            Q20=makeQuery(id+"F1.opExtrude","SWEPT_FACE",FACE,{"disambiguationData":[OSD([sQuery(id+"F0.wireOp",EDGE,"E109.trimOffspring")])]});
            var Q21;
            Q21=makeQuery(id+"F1.opExtrude","SWEPT_FACE",FACE,{"disambiguationData":[OSD([sQuery(id+"F0.wireOp",EDGE,"E110.trimOffspring")])]});
            var Q22;
            Q22=makeQuery(id+"F1.opExtrude","SWEPT_FACE",FACE,{"disambiguationData":[OSD([sQuery(id+"F0.wireOp",EDGE,"E57")])]});
            chamfer(context, id + "F2", {"entities" : qUnion([Q0, Q1, Q2, Q3, Q4, Q5, Q6, Q7, Q8, Q9, Q10, Q11, Q12, Q13, Q14, Q15, Q16, Q17, Q18, Q19, Q20, Q21, Q22]), "width" : 0.13 * mm, "tangentPropagation" : true});
        }
    });
